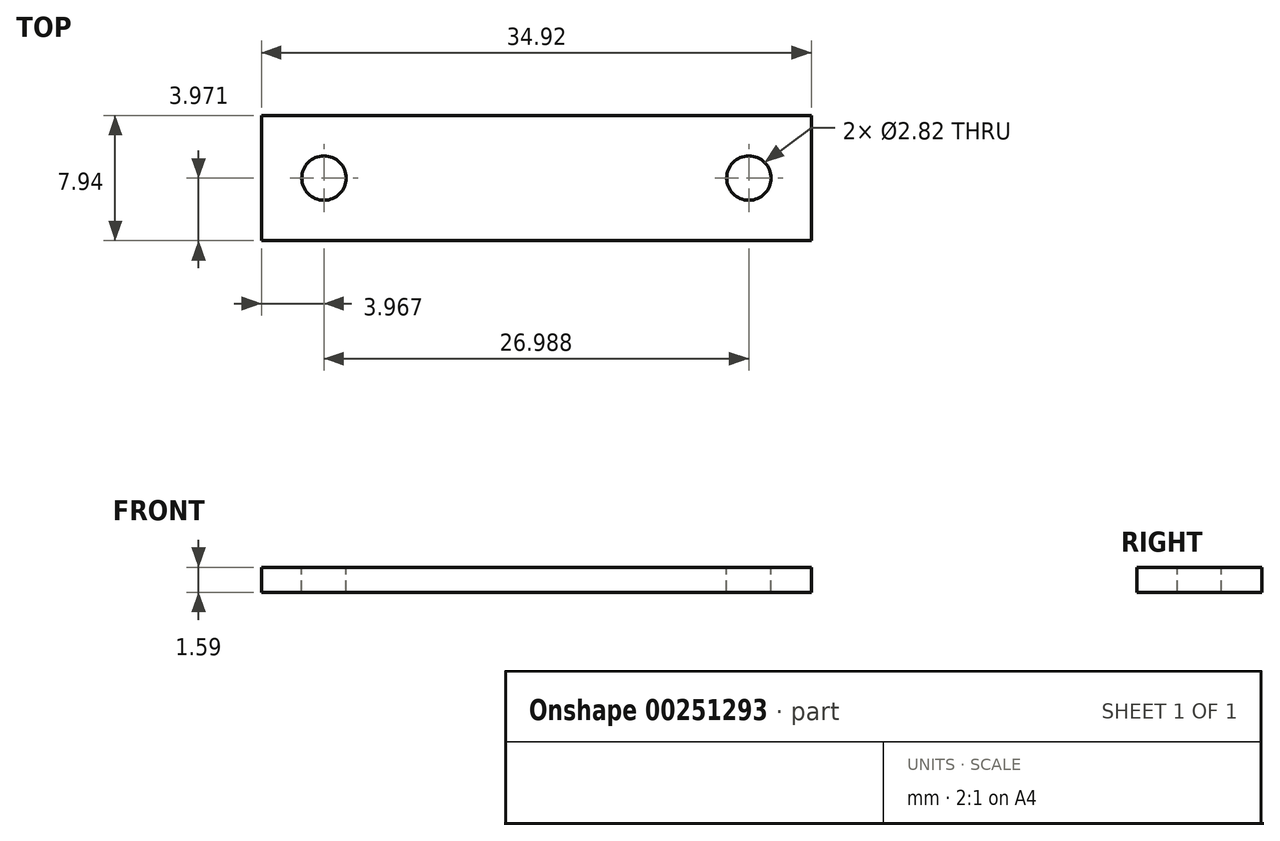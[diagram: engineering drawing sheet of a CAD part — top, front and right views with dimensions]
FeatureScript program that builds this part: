
annotation { "Feature Type Name" : "Feature", "Feature Type Description" : "" }
export const myFeature = defineFeature(function(context is Context, id is Id, definition is map)
    precondition{}
    {
        {
            var Q0;
            Q0=qCreatedBy(makeId("Front.planeOp"),FACE);
            var sketch = newSketch(context, id + "F0", { "sketchPlane" : qUnion([Q0])});
            skLineSegment(sketch, "E0.bottom", {"start": v(10.1, 10.1) * mm, "end": v(45.02, 10.1) * mm});
            skLineSegment(sketch, "E0.top", {"start": v(10.1, 11.69) * mm, "end": v(45.02, 11.69) * mm});
            skLineSegment(sketch, "E0.left", {"start": v(10.1, 10.1) * mm, "end": v(10.1, 11.69) * mm});
            skLineSegment(sketch, "E0.right", {"start": v(45.02, 10.1) * mm, "end": v(45.02, 11.69) * mm});
            skSolve(sketch);
        }
        {
            var Q0;
            Q0 = qSketchRegion(id + "F0", true);
            extrude(context, id + "F1", {"entities" : qUnion([Q0]), "depth" : 7.94 * mm});
        }
        {
            var Q0;
            Q0=makeQuery(id+"F1.opExtrude","SWEPT_FACE",FACE,{"disambiguationData":[OSD([sQuery(id+"F0.wireOp",EDGE,"E0.top")])]});
            var sketch = newSketch(context, id + "F2", { "sketchPlane" : qUnion([Q0])});
            skCircle(sketch, "E1", {"center": v(14.07, -3.97) * mm, "radius": 1.4 * mm});
            skCircle(sketch, "E2", {"center": v(41.05, -3.97) * mm, "radius": 1.4 * mm});
            skSolve(sketch);
        }
        {
            var Q0;
            Q0 = qSketchRegion(id + "F2", true);
            extrude(context, id + "F3", {"entities" : qUnion([Q0]), "operationType" : NewBodyOperationType.REMOVE, "oppositeDirection" : true, "depth" : 1.59 * mm});
        }
    });
